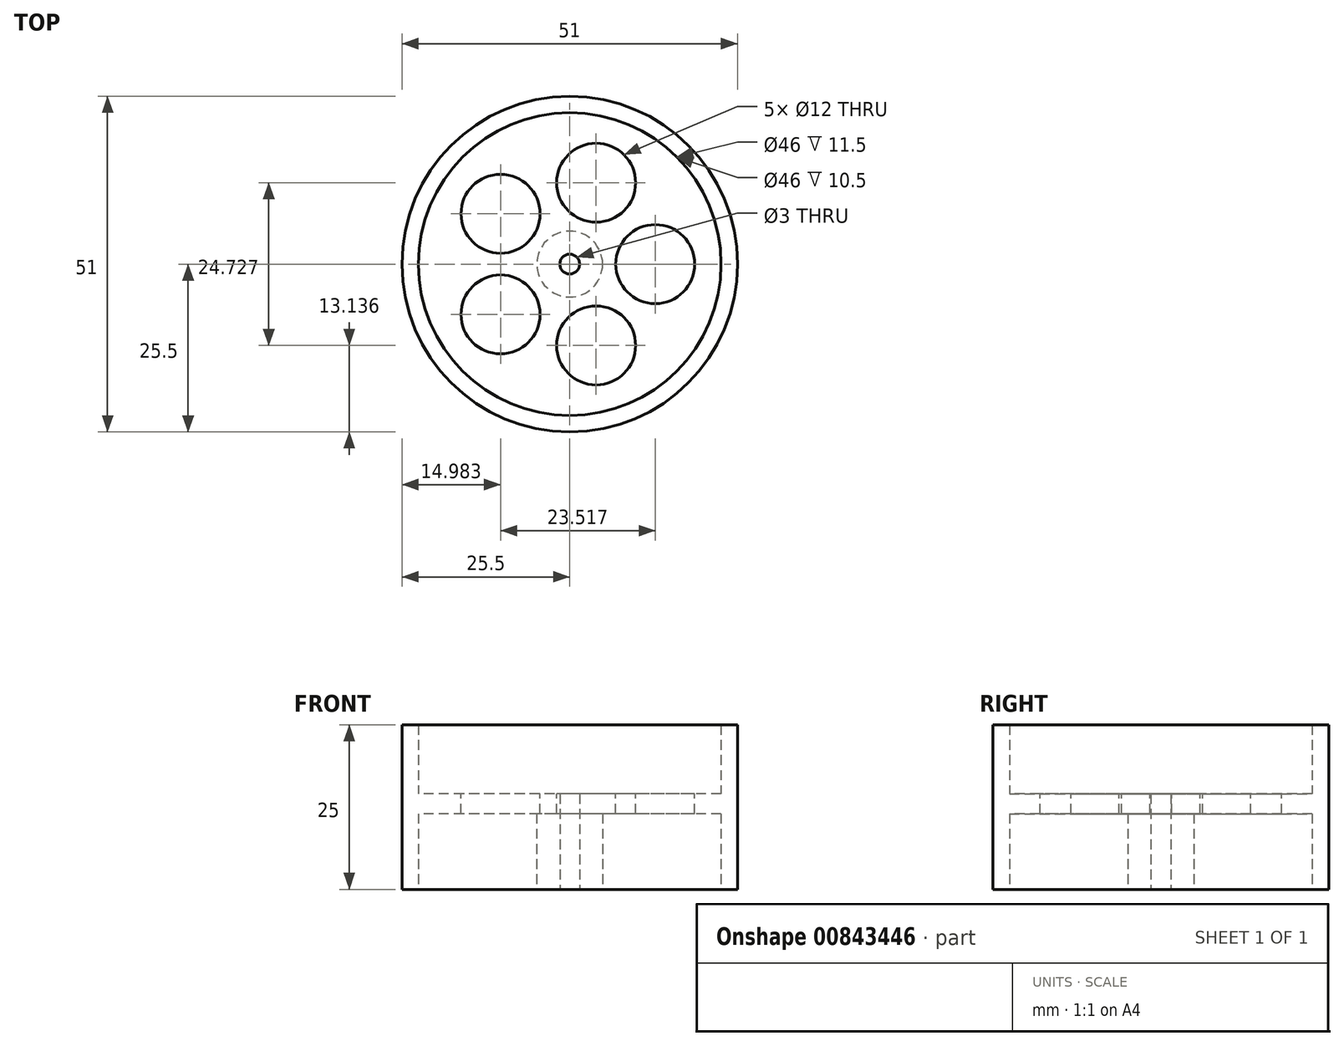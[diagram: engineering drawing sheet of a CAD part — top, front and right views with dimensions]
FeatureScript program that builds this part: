
annotation { "Feature Type Name" : "Feature", "Feature Type Description" : "" }
export const myFeature = defineFeature(function(context is Context, id is Id, definition is map)
    precondition{}
    {
        {
            var Q0;
            Q0=qCreatedBy(makeId("Top.planeOp"),FACE);
            var sketch = newSketch(context, id + "F0", { "sketchPlane" : qUnion([Q0])});
            skCircle(sketch, "E0", {"center": v(0, 0) * mm, "radius": 25.5 * mm});
            skCircle(sketch, "E1", {"center": v(0, 0) * mm, "radius": 23 * mm});
            skSolve(sketch);
        }
        {
            var Q0;
            Q0=qCreatedBy(makeId("Top.planeOp"),FACE);
            var sketch = newSketch(context, id + "F1", { "sketchPlane" : qUnion([Q0])});
            skCircle(sketch, "E2", {"center": v(0, 0) * mm, "radius": 5 * mm});
            skCircle(sketch, "E3", {"center": v(0, 0) * mm, "radius": 1.5 * mm});
            skSolve(sketch);
        }
        {
            var Q0;
            Q0 = qSketchRegion(id + "F0", true);
            extrude(context, id + "F2", {"entities" : qUnion([Q0]), "depth" : 25 * mm, "offsetDistance" : 25 * mm});
        }
        {
            var Q0;
            Q0 = qSketchRegion(id + "F1", true);
            extrude(context, id + "F3", {"entities" : qUnion([Q0]), "depth" : 14.5 * mm, "offsetDistance" : 25 * mm});
        }
        {
            var Q0;
            Q0=makeQuery(id+"F3.opExtrude","CAP_FACE",FACE,{"disambiguationData":[OSD([sQuery(id+"F1.wireOp",EDGE,"E2"),sQuery(id+"F1.wireOp",EDGE,"E3")])],"isStart":false});
            var sketch = newSketch(context, id + "F4", { "sketchPlane" : qUnion([Q0])});
            skCircle(sketch, "E4", {"center": v(0, 0) * mm, "radius": 23 * mm});
            skCircle(sketch, "E5.cCircle", {"center": v(0, 0) * mm, "radius": 13 * mm, "construction": true});
            skLineSegment(sketch, "E5.0", {"start": v(13, 0) * mm, "end": v(4.02, -12.36) * mm});
            skLineSegment(sketch, "E5.1", {"start": v(4.02, -12.36) * mm, "end": v(-10.52, -7.64) * mm});
            skLineSegment(sketch, "E5.2", {"start": v(-10.52, -7.64) * mm, "end": v(-10.52, 7.64) * mm});
            skLineSegment(sketch, "E5.3", {"start": v(-10.52, 7.64) * mm, "end": v(4.02, 12.36) * mm});
            skLineSegment(sketch, "E5.4", {"start": v(4.02, 12.36) * mm, "end": v(13, 0) * mm});
            skCircle(sketch, "E6", {"center": v(4.02, 12.36) * mm, "radius": 6 * mm});
            skCircle(sketch, "E7", {"center": v(13, 0) * mm, "radius": 6 * mm});
            skCircle(sketch, "E8", {"center": v(-10.52, 7.64) * mm, "radius": 6 * mm});
            skCircle(sketch, "E9", {"center": v(-10.52, -7.64) * mm, "radius": 6 * mm});
            skCircle(sketch, "E10", {"center": v(4.02, -12.36) * mm, "radius": 6 * mm});
            skSolve(sketch);
        }
        {
            var Q0;
            Q0=makeQuery(id+"F4.imprint","IMPRINT",FACE,{"disambiguationData":[TD([[makeQuery(id+"F4.imprint","IMPRINT",EDGE,{"derivedFrom":sQuery(id+"F4.wireOp",EDGE,"E4")}),1.0]])]});
            var Q1;
            Q1=makeQuery(id+"F4.imprint","IMPRINT",FACE,{"disambiguationData":[TD([[makeQuery(id+"F4.imprint","IMPRINT",EDGE,{"derivedFrom":makeQuery(id+"F3.opExtrude","CAP_EDGE",EDGE,{"disambiguationData":[OSD([sQuery(id+"F1.wireOp",EDGE,"E2")])],"isStart":false})}),-1.0]])]});
            extrude(context, id + "F5", {"entities" : qUnion([Q0, Q1]), "operationType" : NewBodyOperationType.ADD, "depth" : -3 * mm, "offsetDistance" : 25 * mm});
        }
    });
